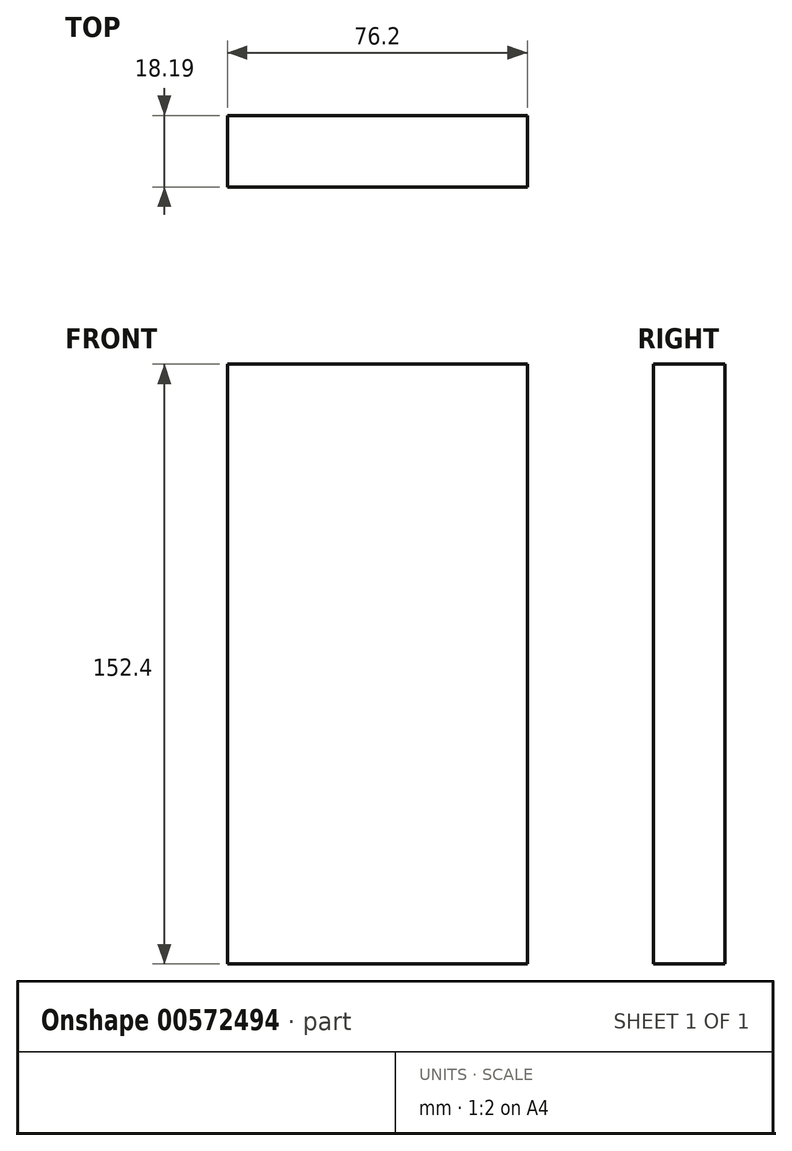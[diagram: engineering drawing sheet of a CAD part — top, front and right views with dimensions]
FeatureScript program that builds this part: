
annotation { "Feature Type Name" : "Feature", "Feature Type Description" : "" }
export const myFeature = defineFeature(function(context is Context, id is Id, definition is map)
    precondition{}
    {
        {
            var Q0;
            Q0=qCreatedBy(makeId("Front.planeOp"),FACE);
            var sketch = newSketch(context, id + "F0", { "sketchPlane" : qUnion([Q0])});
            skLineSegment(sketch, "E0", {"start": v(-13.35, 73.37) * mm, "end": v(62.85, 73.37) * mm});
            skLineSegment(sketch, "E1", {"start": v(62.85, 73.37) * mm, "end": v(62.85, -79.03) * mm});
            skLineSegment(sketch, "E2", {"start": v(62.85, -79.03) * mm, "end": v(-13.35, -79.03) * mm});
            skLineSegment(sketch, "E3", {"start": v(-13.35, -79.03) * mm, "end": v(-13.35, 73.37) * mm});
            skSolve(sketch);
        }
        {
            var Q0;
            Q0=makeQuery(id+"F0.imprint","IMPRINT",FACE,{"disambiguationData":[TD([[makeQuery(id+"F0.imprint","IMPRINT",EDGE,{"derivedFrom":sQuery(id+"F0.wireOp",EDGE,"E0")}),-1.0]])]});
            extrude(context, id + "F1", {"entities" : qUnion([Q0]), "depth" : 18.2 * mm, "offsetDistance" : 25.4 * mm});
        }
    });
